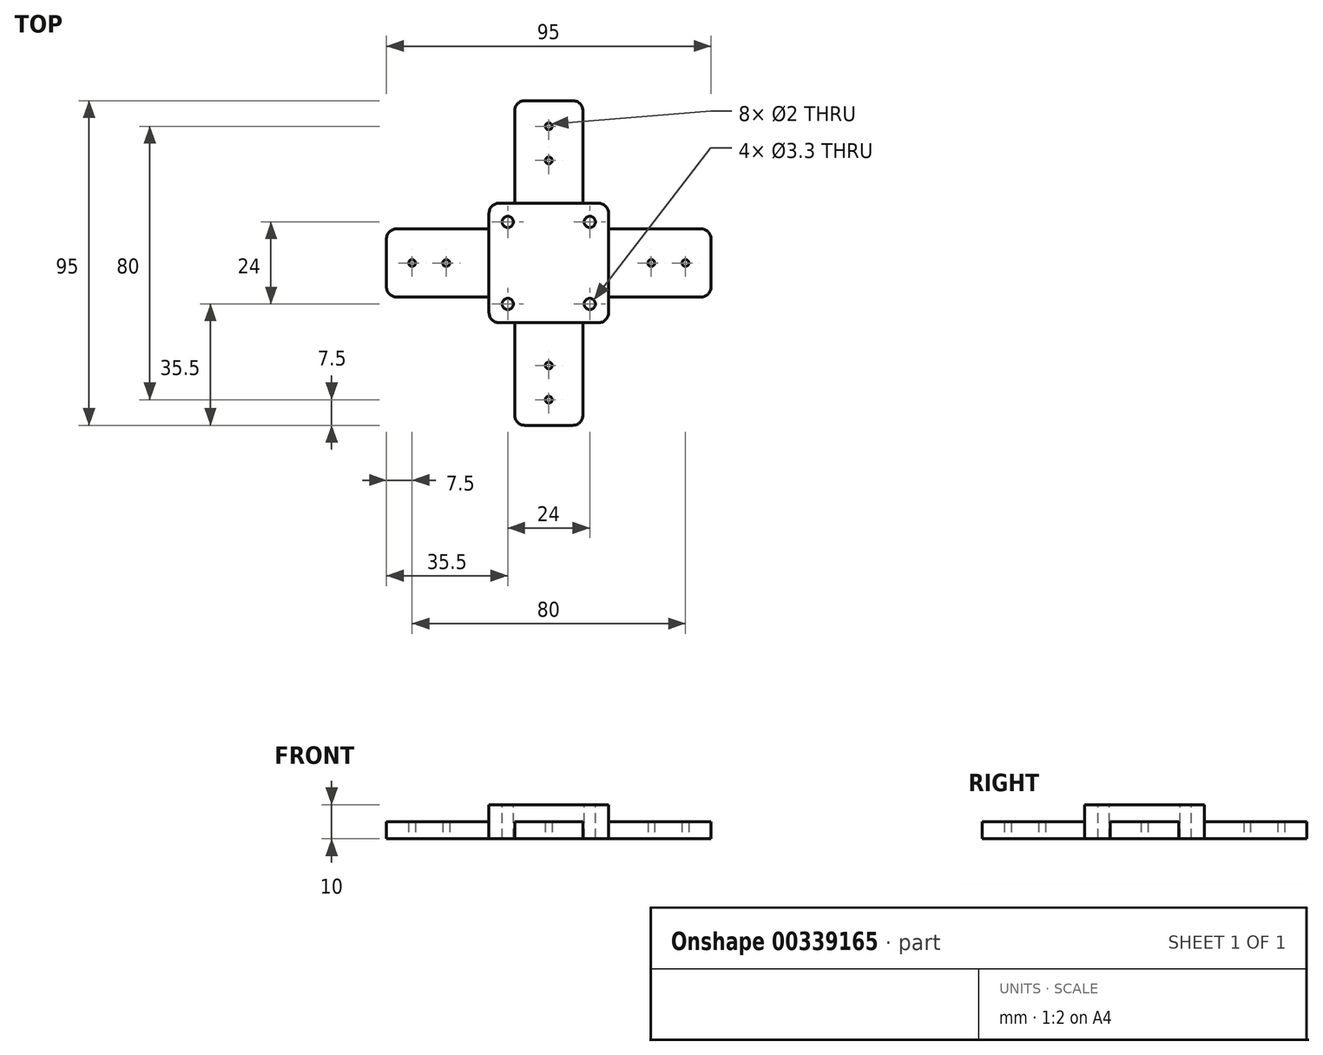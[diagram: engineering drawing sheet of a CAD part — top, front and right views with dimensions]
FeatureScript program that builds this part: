
annotation { "Feature Type Name" : "Feature", "Feature Type Description" : "" }
export const myFeature = defineFeature(function(context is Context, id is Id, definition is map)
    precondition{}
    {
        {
            var Q0;
            Q0=qCreatedBy(makeId("Top.planeOp"),FACE);
            cPlane(context, id + "F0", {"entities" : qUnion([Q0]), "cplaneType" : CPlaneType.OFFSET, "offset" : 9 * mm, "width" : 150 * mm, "height" : 150 * mm});
        }
        {
            var Q0;
            Q0=qCreatedBy(id+"F0.planeOp",FACE);
            var sketch = newSketch(context, id + "F1", { "sketchPlane" : qUnion([Q0])});
            skLineSegment(sketch, "E0.bottom", {"start": v(17.5, 17.5) * mm, "end": v(-17.5, 17.5) * mm});
            skLineSegment(sketch, "E0.top", {"start": v(17.5, -17.5) * mm, "end": v(-17.5, -17.5) * mm});
            skLineSegment(sketch, "E0.left", {"start": v(17.5, 17.5) * mm, "end": v(17.5, -17.5) * mm});
            skLineSegment(sketch, "E0.right", {"start": v(-17.5, 17.5) * mm, "end": v(-17.5, -17.5) * mm});
            skPoint(sketch, "E0.middle", {"position": v(0, 0) * mm});
            skSolve(sketch);
        }
        {
            var Q0;
            Q0 = qSketchRegion(id + "F1", true);
            extrude(context, id + "F2", {"entities" : qUnion([Q0]), "depth" : 10 * mm});
        }
        {
            var Q0;
            {var subQ0=sQuery(id+"F1.wireOp",EDGE,"E0.right");var subQ1=sQuery(id+"F1.wireOp",EDGE,"E0.top");Q0=makeQuery(id+"F2.opExtrude","SWEPT_EDGE",EDGE,{"disambiguationData":[OSD([subQ1,subQ0]),TDD([makeQuery(id+"F1.imprint","INTERSECT",VERTEX,{"derivedFrom":[subQ1,subQ0]})])]});}
            var Q1;
            Q1=makeQuery(id+"Fl1ss7NW7Q2RMzJ_0.opLoft","SWEPT_EDGE",EDGE,{"disambiguationData":[OSD([sQuery(id+"FNiXv8maSDhl9u7_0.wireOp",EDGE,"w9efNhRJ-STrV-9C2y-wQHD-EQV0Y5t22CGX.top"),sQuery(id+"FNiXv8maSDhl9u7_0.wireOp",EDGE,"w9efNhRJ-STrV-9C2y-wQHD-EQV0Y5t22CGX.right"),sQuery(id+"F1.wireOp",EDGE,"E0.top"),sQuery(id+"F1.wireOp",EDGE,"E0.right")])]});
            var Q2;
            {var subQ0=sQuery(id+"F1.wireOp",EDGE,"E0.left");var subQ1=sQuery(id+"F1.wireOp",EDGE,"E0.top");Q2=makeQuery(id+"F2.opExtrude","SWEPT_EDGE",EDGE,{"disambiguationData":[OSD([subQ1,subQ0]),TDD([makeQuery(id+"F1.imprint","INTERSECT",VERTEX,{"derivedFrom":[subQ1,subQ0]})])]});}
            var Q3;
            Q3=makeQuery(id+"Fl1ss7NW7Q2RMzJ_0.opLoft","SWEPT_EDGE",EDGE,{"disambiguationData":[OSD([sQuery(id+"FNiXv8maSDhl9u7_0.wireOp",EDGE,"w9efNhRJ-STrV-9C2y-wQHD-EQV0Y5t22CGX.top"),sQuery(id+"FNiXv8maSDhl9u7_0.wireOp",EDGE,"w9efNhRJ-STrV-9C2y-wQHD-EQV0Y5t22CGX.left"),sQuery(id+"F1.wireOp",EDGE,"E0.top"),sQuery(id+"F1.wireOp",EDGE,"E0.left")])]});
            var Q4;
            {var subQ0=sQuery(id+"F1.wireOp",EDGE,"E0.left");var subQ1=sQuery(id+"F1.wireOp",EDGE,"E0.bottom");Q4=makeQuery(id+"F2.opExtrude","SWEPT_EDGE",EDGE,{"disambiguationData":[OSD([subQ1,subQ0]),TDD([makeQuery(id+"F1.imprint","INTERSECT",VERTEX,{"derivedFrom":[subQ1,subQ0]})])]});}
            var Q5;
            Q5=makeQuery(id+"Fl1ss7NW7Q2RMzJ_0.opLoft","SWEPT_EDGE",EDGE,{"disambiguationData":[OSD([sQuery(id+"FNiXv8maSDhl9u7_0.wireOp",EDGE,"w9efNhRJ-STrV-9C2y-wQHD-EQV0Y5t22CGX.bottom"),sQuery(id+"FNiXv8maSDhl9u7_0.wireOp",EDGE,"w9efNhRJ-STrV-9C2y-wQHD-EQV0Y5t22CGX.left"),sQuery(id+"F1.wireOp",EDGE,"E0.bottom"),sQuery(id+"F1.wireOp",EDGE,"E0.left")])]});
            var Q6;
            {var subQ0=sQuery(id+"F1.wireOp",EDGE,"E0.right");var subQ1=sQuery(id+"F1.wireOp",EDGE,"E0.bottom");Q6=makeQuery(id+"F2.opExtrude","SWEPT_EDGE",EDGE,{"disambiguationData":[OSD([subQ1,subQ0]),TDD([makeQuery(id+"F1.imprint","INTERSECT",VERTEX,{"derivedFrom":[subQ1,subQ0]})])]});}
            var Q7;
            Q7=makeQuery(id+"Fl1ss7NW7Q2RMzJ_0.opLoft","SWEPT_EDGE",EDGE,{"disambiguationData":[OSD([sQuery(id+"FNiXv8maSDhl9u7_0.wireOp",EDGE,"w9efNhRJ-STrV-9C2y-wQHD-EQV0Y5t22CGX.bottom"),sQuery(id+"FNiXv8maSDhl9u7_0.wireOp",EDGE,"w9efNhRJ-STrV-9C2y-wQHD-EQV0Y5t22CGX.right"),sQuery(id+"F1.wireOp",EDGE,"E0.bottom"),sQuery(id+"F1.wireOp",EDGE,"E0.right")])]});
            fillet(context, id + "F3", {"entities" : qUnion([Q0, Q1, Q2, Q3, Q4, Q5, Q6, Q7]), "radius" : 3 * mm, "tangentPropagation" : true, "allowEdgeOverflow" : false});
        }
        {
            var Q0;
            Q0=qCreatedBy(id+"F0.planeOp",FACE);
            var sketch = newSketch(context, id + "F4", { "sketchPlane" : qUnion([Q0])});
            skLineSegment(sketch, "E1.bottom", {"start": v(-17.5, 10) * mm, "end": v(-47.5, 10) * mm});
            skLineSegment(sketch, "E1.top", {"start": v(-17.5, -10) * mm, "end": v(-47.5, -10) * mm});
            skLineSegment(sketch, "E1.left", {"start": v(-17.5, 10) * mm, "end": v(-17.5, -10) * mm});
            skLineSegment(sketch, "E1.right", {"start": v(-47.5, 10) * mm, "end": v(-47.5, -10) * mm});
            skPoint(sketch, "E2", {"position": v(-17.5, 0) * mm});
            skLineSegment(sketch, "E3.1.0", {"start": v(-10, -17.5) * mm, "end": v(-10, -47.5) * mm});
            skLineSegment(sketch, "E3.1.1", {"start": v(10, -17.5) * mm, "end": v(10, -47.5) * mm});
            skLineSegment(sketch, "E3.1.2", {"start": v(-10, -47.5) * mm, "end": v(10, -47.5) * mm});
            skLineSegment(sketch, "E3.1.3", {"start": v(-10, -17.5) * mm, "end": v(10, -17.5) * mm});
            skLineSegment(sketch, "E3.2.0", {"start": v(17.5, -10) * mm, "end": v(47.5, -10) * mm});
            skLineSegment(sketch, "E3.2.1", {"start": v(17.5, 10) * mm, "end": v(47.5, 10) * mm});
            skLineSegment(sketch, "E3.2.2", {"start": v(47.5, -10) * mm, "end": v(47.5, 10) * mm});
            skLineSegment(sketch, "E3.2.3", {"start": v(17.5, -10) * mm, "end": v(17.5, 10) * mm});
            skLineSegment(sketch, "E3.3.0", {"start": v(10, 17.5) * mm, "end": v(10, 47.5) * mm});
            skLineSegment(sketch, "E3.3.1", {"start": v(-10, 17.5) * mm, "end": v(-10, 47.5) * mm});
            skLineSegment(sketch, "E3.3.2", {"start": v(10, 47.5) * mm, "end": v(-10, 47.5) * mm});
            skLineSegment(sketch, "E3.3.3", {"start": v(10, 17.5) * mm, "end": v(-10, 17.5) * mm});
            skPoint(sketch, "E3.center", {"position": v(0, 0) * mm});
            skCircle(sketch, "E4", {"center": v(-40, 0) * mm, "radius": 1 * mm});
            skCircle(sketch, "E5", {"center": v(-30, 0) * mm, "radius": 1 * mm});
            skCircle(sketch, "E6.1.1", {"center": v(0, 30) * mm, "radius": 1 * mm});
            skCircle(sketch, "E6.1.2", {"center": v(0, 40) * mm, "radius": 1 * mm});
            skCircle(sketch, "E6.2.1", {"center": v(30, 0) * mm, "radius": 1 * mm});
            skCircle(sketch, "E6.2.2", {"center": v(40, 0) * mm, "radius": 1 * mm});
            skCircle(sketch, "E6.3.1", {"center": v(0, -30) * mm, "radius": 1 * mm});
            skCircle(sketch, "E6.3.2", {"center": v(0, -40) * mm, "radius": 1 * mm});
            skLineSegment(sketch, "E6.anchor1", {"start": v(0, 0) * mm, "end": v(-30, 0) * mm, "construction": true});
            skLineSegment(sketch, "E6.anchor2", {"start": v(0, 0) * mm, "end": v(0, -30) * mm, "construction": true});
            skSolve(sketch);
        }
        {
            var Q0;
            Q0=makeQuery(id+"F4.imprint","IMPRINT",FACE,{"disambiguationData":[TD([[makeQuery(id+"F4.imprint","IMPRINT",EDGE,{"derivedFrom":sQuery(id+"F4.wireOp",EDGE,"E3.2.0")}),1.0]])]});
            var Q1;
            Q1 = qSketchRegion(id + "F4", true);
            extrude(context, id + "F5", {"entities" : qUnion([Q0, Q1]), "operationType" : NewBodyOperationType.ADD, "depth" : 5 * mm});
        }
        {
            var Q0;
            Q0=makeQuery(id+"F5.opExtrude","SWEPT_EDGE",EDGE,{"disambiguationData":[OSD([sQuery(id+"F4.wireOp",EDGE,"E1.bottom"),sQuery(id+"F4.wireOp",EDGE,"E1.right")])]});
            var Q1;
            Q1=makeQuery(id+"F5.opExtrude","SWEPT_EDGE",EDGE,{"disambiguationData":[OSD([sQuery(id+"F4.wireOp",EDGE,"E1.top"),sQuery(id+"F4.wireOp",EDGE,"E1.right")])]});
            var Q2;
            Q2=makeQuery(id+"F5.opExtrude","SWEPT_EDGE",EDGE,{"disambiguationData":[OSD([sQuery(id+"F4.wireOp",EDGE,"E3.1.0"),sQuery(id+"F4.wireOp",EDGE,"E3.1.2")])]});
            var Q3;
            Q3=makeQuery(id+"F5.opExtrude","SWEPT_EDGE",EDGE,{"disambiguationData":[OSD([sQuery(id+"F4.wireOp",EDGE,"E3.1.1"),sQuery(id+"F4.wireOp",EDGE,"E3.1.2")])]});
            var Q4;
            Q4=makeQuery(id+"F5.opExtrude","SWEPT_EDGE",EDGE,{"disambiguationData":[OSD([sQuery(id+"F4.wireOp",EDGE,"E3.2.0"),sQuery(id+"F4.wireOp",EDGE,"E3.2.2")])]});
            var Q5;
            Q5=makeQuery(id+"F5.opExtrude","SWEPT_EDGE",EDGE,{"disambiguationData":[OSD([sQuery(id+"F4.wireOp",EDGE,"E3.2.1"),sQuery(id+"F4.wireOp",EDGE,"E3.2.2")])]});
            var Q6;
            Q6=makeQuery(id+"F5.opExtrude","SWEPT_EDGE",EDGE,{"disambiguationData":[OSD([sQuery(id+"F4.wireOp",EDGE,"E3.3.0"),sQuery(id+"F4.wireOp",EDGE,"E3.3.2")])]});
            var Q7;
            Q7=makeQuery(id+"F5.opExtrude","SWEPT_EDGE",EDGE,{"disambiguationData":[OSD([sQuery(id+"F4.wireOp",EDGE,"E3.3.1"),sQuery(id+"F4.wireOp",EDGE,"E3.3.2")])]});
            fillet(context, id + "F6", {"entities" : qUnion([Q0, Q1, Q2, Q3, Q4, Q5, Q6, Q7]), "radius" : 3 * mm, "tangentPropagation" : true, "allowEdgeOverflow" : false});
        }
        {
            var Q0;
            Q0=makeQuery(id+"F2.opExtrude","CAP_FACE",FACE,{"disambiguationData":[OSD([sQuery(id+"F1.wireOp",EDGE,"E0.bottom"),sQuery(id+"F1.wireOp",EDGE,"E0.top"),sQuery(id+"F1.wireOp",EDGE,"E0.left"),sQuery(id+"F1.wireOp",EDGE,"E0.right")])],"isStart":false});
            var sketch = newSketch(context, id + "F7", { "sketchPlane" : qUnion([Q0])});
            skCircle(sketch, "E7", {"center": v(-12, 12) * mm, "radius": 1.65 * mm});
            skCircle(sketch, "E8.1.0", {"center": v(-12, -12) * mm, "radius": 1.65 * mm});
            skCircle(sketch, "E8.2.0", {"center": v(12, -12) * mm, "radius": 1.65 * mm});
            skCircle(sketch, "E8.3.0", {"center": v(12, 12) * mm, "radius": 1.65 * mm});
            skPoint(sketch, "E8.center", {"position": v(0, 0) * mm});
            skSolve(sketch);
        }
        {
            var Q0;
            Q0=sQuery(id+"F7.wireOp",VERTEX,"E7.center");
            var Q1;
            Q1=sQuery(id+"F7.wireOp",VERTEX,"E8.3.0.center");
            var Q2;
            Q2=sQuery(id+"F7.wireOp",VERTEX,"E8.2.0.center");
            var Q3;
            Q3=sQuery(id+"F7.wireOp",VERTEX,"E8.1.0.center");
            var Q4;
            Q4=makeQuery(id+"F2.opExtrude","SWEPT_BODY",BODY,{"disambiguationData":[OSD([sQuery(id+"F1.wireOp",EDGE,"E0.bottom"),sQuery(id+"F1.wireOp",EDGE,"E0.top"),sQuery(id+"F1.wireOp",EDGE,"E0.left"),sQuery(id+"F1.wireOp",EDGE,"E0.right")])]});
            hole(context, id + "F8", {"style" : HoleStyle.SIMPLE, "endStyle" : HoleEndStyle.THROUGH, "holeDiameter" : 3.3 * mm, "tappedDepth" : 12 * mm, "tapClearance" : 3, "locations" : qUnion([Q0, Q1, Q2, Q3]), "scope" : qUnion([Q4])});
        }
    });
